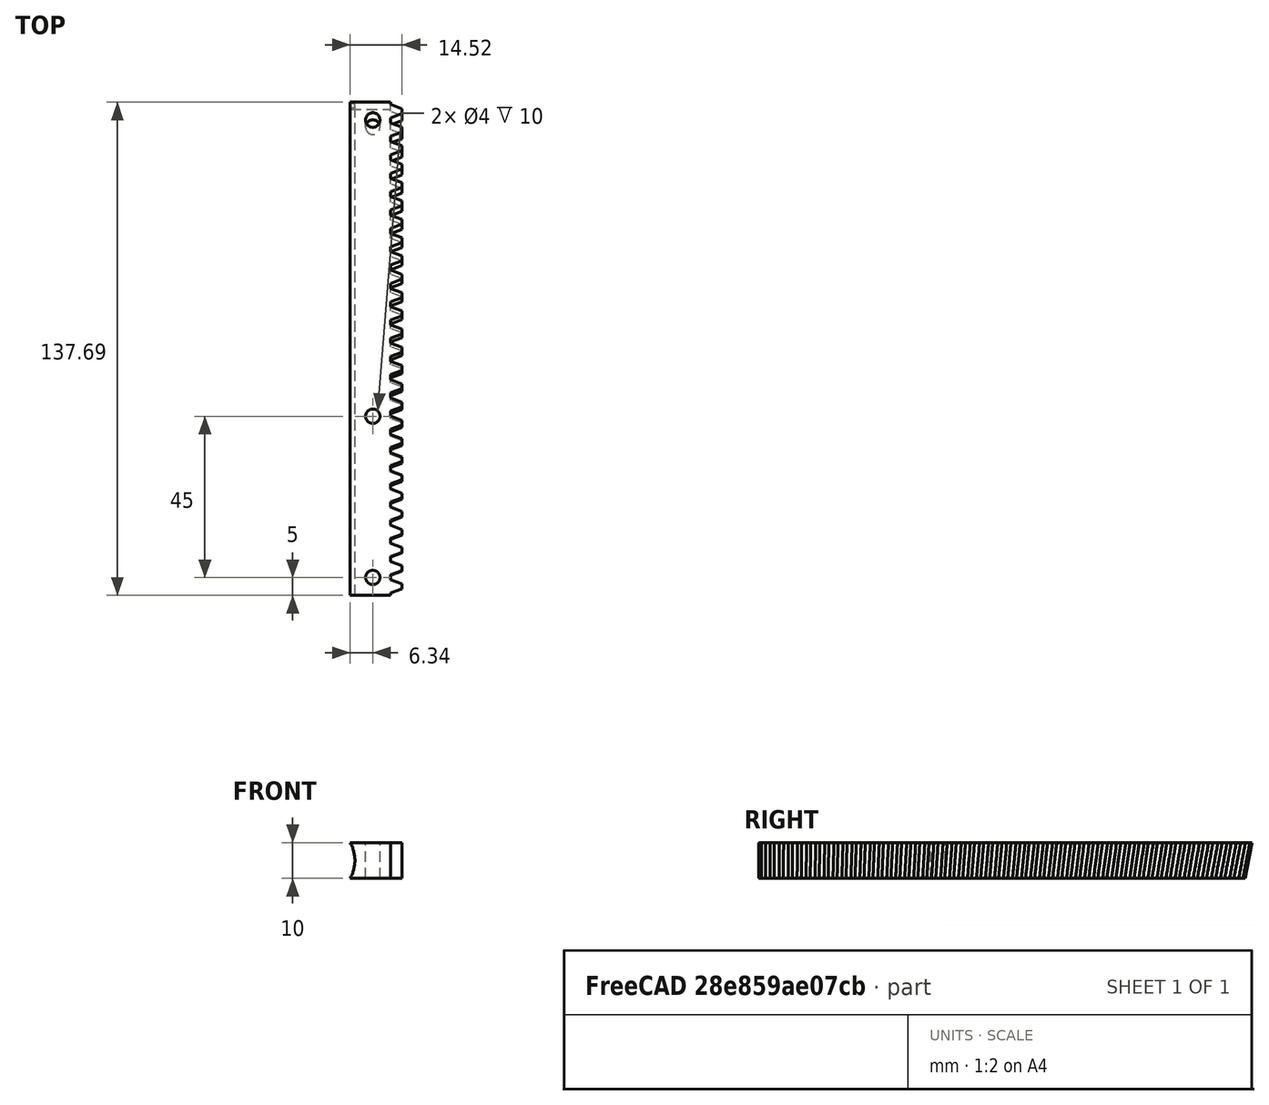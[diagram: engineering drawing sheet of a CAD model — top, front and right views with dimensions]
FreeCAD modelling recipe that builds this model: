
FCSTD DOCUMENT  (FreeCAD 0.17R13522 (Git))
Label: turnrack
License: All rights reserved
LicenseURL: http://en.wikipedia.org/wiki/All_rights_reserved
objects: Part::FeaturePython×27, Part::Cylinder×5, Part::MultiFuse×3, Part::Box×2, Part::Cut×1
note: 38 computed .brp shape members not serialized (recipe doc carries the construction recipe); baked Part::Feature solids carry a one-line shape summary decoded from their .brp

FEATURE [Part::FeaturePython] InvoluteRack  # WARN: FeaturePython — macro-defined, semantics opaque (R4)
  beta = 0
  double_helix = false
  head = 0
  height = 10
  module = 1.59155
  pressure_angle = 20
  teeth = 1
  thickness = 10
FEATURE [Part::FeaturePython] InvoluteRack001  # WARN: FeaturePython — macro-defined, semantics opaque (R4)
  Placement = pos=(0,5,0) rot=(0,0,1;0rad)
  beta = 0.416667
  double_helix = false
  head = 0
  height = 10
  module = 1.59155
  pressure_angle = 20
  teeth = 1
  thickness = 10
FEATURE [Part::FeaturePython] InvoluteRack002  # WARN: FeaturePython — macro-defined, semantics opaque (R4)
  Placement = pos=(0,10.0001,0) rot=(0,0,1;0rad)
  beta = 0.833333
  double_helix = false
  head = 0
  height = 10
  module = 1.59155
  pressure_angle = 20
  teeth = 1
  thickness = 10
FEATURE [Part::FeaturePython] InvoluteRack003  # WARN: FeaturePython — macro-defined, semantics opaque (R4)
  Placement = pos=(0,15.0007,0) rot=(0,0,1;0rad)
  beta = 1.25
  double_helix = false
  head = 0
  height = 10
  module = 1.59155
  pressure_angle = 20
  teeth = 1
  thickness = 10
FEATURE [Part::FeaturePython] InvoluteRack004  # WARN: FeaturePython — macro-defined, semantics opaque (R4)
  Placement = pos=(0,20.0019,0) rot=(0,0,1;0rad)
  beta = 1.66667
  double_helix = false
  head = 0
  height = 10
  module = 1.59155
  pressure_angle = 20
  teeth = 1
  thickness = 10
FEATURE [Part::FeaturePython] InvoluteRack005  # WARN: FeaturePython — macro-defined, semantics opaque (R4)
  Placement = pos=(0,25.004,0) rot=(0,0,1;0rad)
  beta = 2.08333
  double_helix = false
  head = 0
  height = 10
  module = 1.59155
  pressure_angle = 20
  teeth = 1
  thickness = 10
FEATURE [Part::FeaturePython] InvoluteRack006  # WARN: FeaturePython — macro-defined, semantics opaque (R4)
  Placement = pos=(0,30.0073,0) rot=(0,0,1;0rad)
  beta = 2.5
  double_helix = false
  head = 0
  height = 10
  module = 1.59155
  pressure_angle = 20
  teeth = 1
  thickness = 10
FEATURE [Part::FeaturePython] InvoluteRack007  # WARN: FeaturePython — macro-defined, semantics opaque (R4)
  Placement = pos=(0,35.012,0) rot=(0,0,1;0rad)
  beta = 2.91667
  double_helix = false
  head = 0
  height = 10
  module = 1.59155
  pressure_angle = 20
  teeth = 1
  thickness = 10
FEATURE [Part::FeaturePython] InvoluteRack008  # WARN: FeaturePython — macro-defined, semantics opaque (R4)
  Placement = pos=(0,40.0185,0) rot=(0,0,1;0rad)
  beta = 3.33333
  double_helix = false
  head = 0
  height = 10
  module = 1.59155
  pressure_angle = 20
  teeth = 1
  thickness = 10
FEATURE [Part::FeaturePython] InvoluteRack009  # WARN: FeaturePython — macro-defined, semantics opaque (R4)
  Placement = pos=(0,45.027,0) rot=(0,0,1;0rad)
  beta = 3.75
  double_helix = false
  head = 0
  height = 10
  module = 1.59155
  pressure_angle = 20
  teeth = 1
  thickness = 10
FEATURE [Part::FeaturePython] InvoluteRack010  # WARN: FeaturePython — macro-defined, semantics opaque (R4)
  Placement = pos=(0,50.0377,0) rot=(0,0,1;0rad)
  beta = 4.16667
  double_helix = false
  head = 0
  height = 10
  module = 1.59155
  pressure_angle = 20
  teeth = 1
  thickness = 10
FEATURE [Part::FeaturePython] InvoluteRack011  # WARN: FeaturePython — macro-defined, semantics opaque (R4)
  Placement = pos=(0,55.051,0) rot=(0,0,1;0rad)
  beta = 4.58333
  double_helix = false
  head = 0
  height = 10
  module = 1.59155
  pressure_angle = 20
  teeth = 1
  thickness = 10
FEATURE [Part::FeaturePython] InvoluteRack012  # WARN: FeaturePython — macro-defined, semantics opaque (R4)
  Placement = pos=(0,60.067,0) rot=(0,0,1;0rad)
  beta = 5
  double_helix = false
  head = 0
  height = 10
  module = 1.59155
  pressure_angle = 20
  teeth = 1
  thickness = 10
FEATURE [Part::FeaturePython] InvoluteRack013  # WARN: FeaturePython — macro-defined, semantics opaque (R4)
  Placement = pos=(0,65.0861,0) rot=(0,0,1;0rad)
  beta = 5.41667
  double_helix = false
  head = 0
  height = 10
  module = 1.59155
  pressure_angle = 20
  teeth = 1
  thickness = 10
FEATURE [Part::FeaturePython] InvoluteRack014  # WARN: FeaturePython — macro-defined, semantics opaque (R4)
  Placement = pos=(0,70.1085,0) rot=(0,0,1;0rad)
  beta = 5.83333
  double_helix = false
  head = 0
  height = 10
  module = 1.59155
  pressure_angle = 20
  teeth = 1
  thickness = 10
FEATURE [Part::FeaturePython] InvoluteRack015  # WARN: FeaturePython — macro-defined, semantics opaque (R4)
  Placement = pos=(0,75.1346,0) rot=(0,0,1;0rad)
  beta = 6.25
  double_helix = false
  head = 0
  height = 10
  module = 1.59155
  pressure_angle = 20
  teeth = 1
  thickness = 10
FEATURE [Part::FeaturePython] InvoluteRack016  # WARN: FeaturePython — macro-defined, semantics opaque (R4)
  Placement = pos=(0,80.1645,0) rot=(0,0,1;0rad)
  beta = 6.66667
  double_helix = false
  head = 0
  height = 10
  module = 1.59155
  pressure_angle = 20
  teeth = 1
  thickness = 10
FEATURE [Part::FeaturePython] InvoluteRack017  # WARN: FeaturePython — macro-defined, semantics opaque (R4)
  Placement = pos=(0,85.1985,0) rot=(0,0,1;0rad)
  beta = 7.08333
  double_helix = false
  head = 0
  height = 10
  module = 1.59155
  pressure_angle = 20
  teeth = 1
  thickness = 10
FEATURE [Part::FeaturePython] InvoluteRack018  # WARN: FeaturePython — macro-defined, semantics opaque (R4)
  Placement = pos=(0,90.237,0) rot=(0,0,1;0rad)
  beta = 7.5
  double_helix = false
  head = 0
  height = 10
  module = 1.59155
  pressure_angle = 20
  teeth = 1
  thickness = 10
FEATURE [Part::FeaturePython] InvoluteRack019  # WARN: FeaturePython — macro-defined, semantics opaque (R4)
  Placement = pos=(0,95.2801,0) rot=(0,0,1;0rad)
  beta = 7.91667
  double_helix = false
  head = 0
  height = 10
  module = 1.59155
  pressure_angle = 20
  teeth = 1
  thickness = 10
FEATURE [Part::FeaturePython] InvoluteRack020  # WARN: FeaturePython — macro-defined, semantics opaque (R4)
  Placement = pos=(0,100.328,0) rot=(0,0,1;0rad)
  beta = 8.33333
  double_helix = false
  head = 0
  height = 10
  module = 1.59155
  pressure_angle = 20
  teeth = 1
  thickness = 10
FEATURE [Part::FeaturePython] InvoluteRack021  # WARN: FeaturePython — macro-defined, semantics opaque (R4)
  Placement = pos=(0,105.382,0) rot=(0,0,1;0rad)
  beta = 8.75
  double_helix = false
  head = 0
  height = 10
  module = 1.59155
  pressure_angle = 20
  teeth = 1
  thickness = 10
FEATURE [Part::FeaturePython] InvoluteRack022  # WARN: FeaturePython — macro-defined, semantics opaque (R4)
  Placement = pos=(0,110.44,0) rot=(0,0,1;0rad)
  beta = 9.16667
  double_helix = false
  head = 0
  height = 10
  module = 1.59155
  pressure_angle = 20
  teeth = 1
  thickness = 10
FEATURE [Part::FeaturePython] InvoluteRack023  # WARN: FeaturePython — macro-defined, semantics opaque (R4)
  Placement = pos=(0,115.505,0) rot=(0,0,1;0rad)
  beta = 9.58333
  double_helix = false
  head = 0
  height = 10
  module = 1.59155
  pressure_angle = 20
  teeth = 1
  thickness = 10
FEATURE [Part::FeaturePython] InvoluteRack024  # WARN: FeaturePython — macro-defined, semantics opaque (R4)
  Placement = pos=(0,120.576,0) rot=(0,0,1;0rad)
  beta = 10
  double_helix = false
  head = 0
  height = 10
  module = 1.59155
  pressure_angle = 20
  teeth = 1
  thickness = 10
FEATURE [Part::FeaturePython] InvoluteRack025  # WARN: FeaturePython — macro-defined, semantics opaque (R4)
  Placement = pos=(0,125.653,0) rot=(0,0,1;0rad)
  beta = 10.4167
  double_helix = false
  head = 0
  height = 10
  module = 1.59155
  pressure_angle = 20
  teeth = 1
  thickness = 10
FEATURE [Part::FeaturePython] InvoluteRack026  # WARN: FeaturePython — macro-defined, semantics opaque (R4)
  Placement = pos=(0,130.737,0) rot=(0,0,1;0rad)
  beta = 10.8333
  double_helix = false
  head = 0
  height = 10
  module = 1.59155
  pressure_angle = 20
  teeth = 1
  thickness = 10
FEATURE [Part::MultiFuse] Union  label="Linear Beta Rack"
  Placement = pos=(11.5915,2.5,0) rot=(0,0,1;0rad)
  Shapes = -> [InvoluteRack,InvoluteRack001,InvoluteRack002,InvoluteRack003,InvoluteRack004,InvoluteRack005,InvoluteRack006,InvoluteRack007,InvoluteRack008,InvoluteRack009,InvoluteRack010,InvoluteRack011,InvoluteRack012,InvoluteRack013,InvoluteRack014,InvoluteRack015,InvoluteRack016,InvoluteRack017,InvoluteRack018,InvoluteRack019,InvoluteRack020,InvoluteRack021,InvoluteRack022,InvoluteRack023,InvoluteRack024,+2 more]
  expr: Placement.Base.x = 10 + 5 / pi
FEATURE [Part::Box] Box  label="Cube"
  AttacherType = Attacher::AttachEngine3D
  Height = 10
  Length = 12
  Placement = pos=(-2,0,0) rot=(0,0,1;0rad)
  Width = 138.25
FEATURE [Part::MultiFuse] Fusion  label="Positive Fusion"
  Shapes = -> [Union,Box]
FEATURE [Part::Box] Box001  label="Cut Off Angle Cube"
  AttacherType = Attacher::AttachEngine3D
  Height = 12
  Length = 12
  Placement = pos=(-2,135.7,0) rot=(-1,0,0;0.19635rad)
  Width = 10
FEATURE [Part::Cylinder] Cylinder  label="Screw Mid"
  Angle = 360
  AttacherType = Attacher::AttachEngine3D
  Height = 10
  Placement = pos=(5,50,0) rot=(0,0,1;0rad)
  Radius = 2
FEATURE [Part::Cylinder] Cylinder001  label="Screw End"
  Angle = 360
  AttacherType = Attacher::AttachEngine3D
  Height = 12
  Placement = pos=(5,130.7,0) rot=(-1,0,0;0.19635rad)
  Radius = 2
FEATURE [Part::Cylinder] Cylinder002  label="Screw End 2"
  Angle = 360
  AttacherType = Attacher::AttachEngine3D
  Height = 1
  Placement = pos=(5,130.7,0) rot=(1,0,0;2.94524rad)
  Radius = 2
FEATURE [Part::Cylinder] Cylinder003  label="Rail Cylinder"
  Angle = 360
  AttacherType = Attacher::AttachEngine3D
  Height = 150
  Placement = pos=(-10,0,5) rot=(-1,0,0;1.5708rad)
  Radius = 10
FEATURE [Part::Cylinder] Cylinder004  label="Screw Start"
  Angle = 360
  AttacherType = Attacher::AttachEngine3D
  Height = 10
  Placement = pos=(5,5,0) rot=(0,0,1;0rad)
  Radius = 2
FEATURE [Part::MultiFuse] Fusion001  label="Negative Fusion"
  Shapes = -> [Box001,Cylinder,Cylinder001,Cylinder002,Cylinder003,Cylinder004]
FEATURE [Part::Cut] Cut
  Base = -> Fusion
  Tool = -> Fusion001
